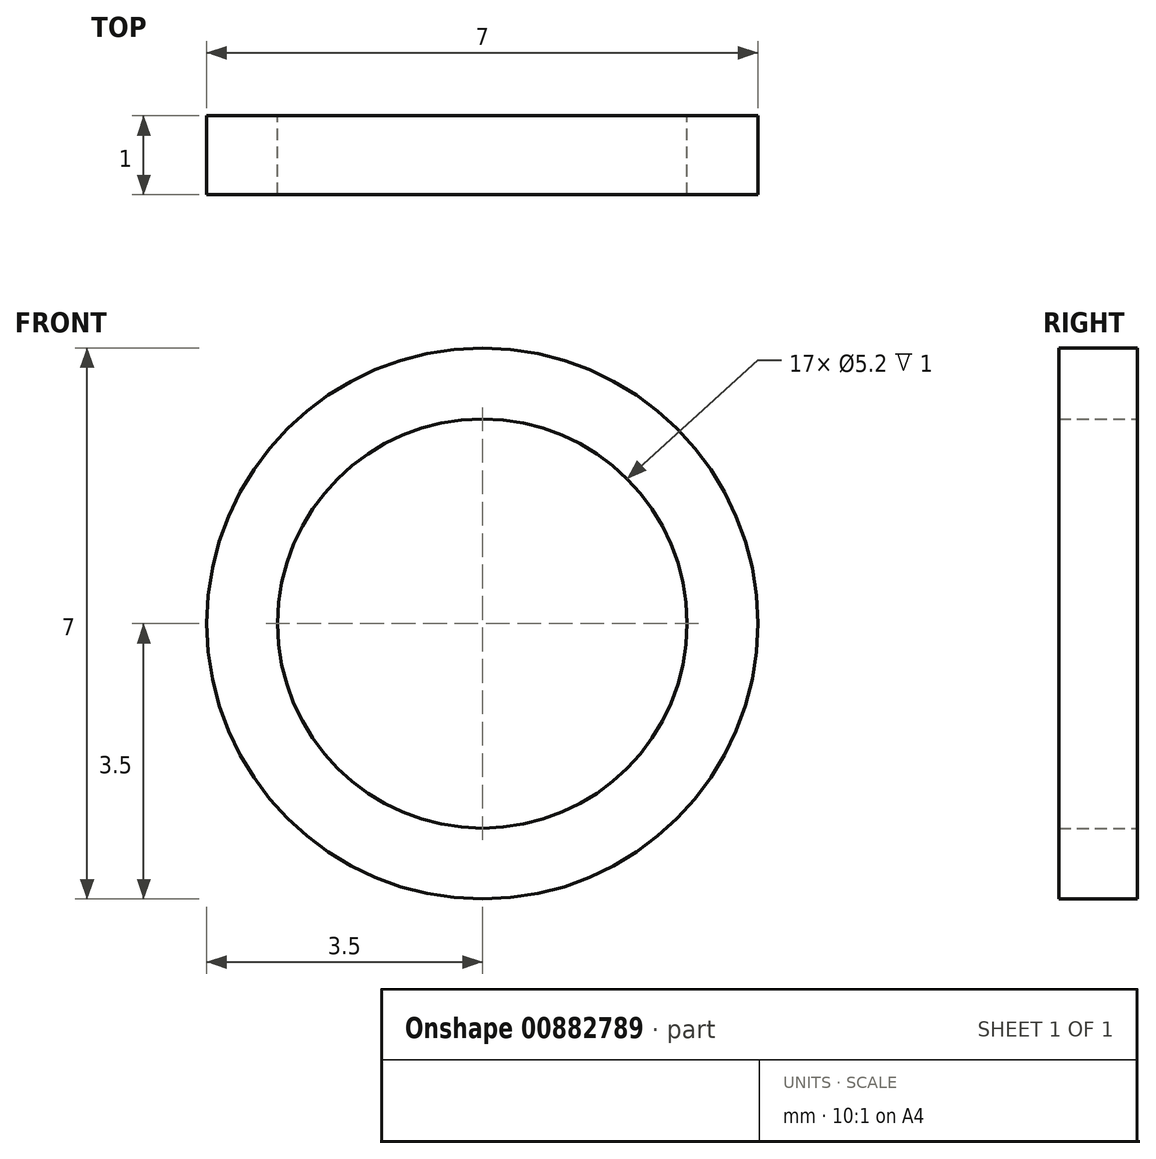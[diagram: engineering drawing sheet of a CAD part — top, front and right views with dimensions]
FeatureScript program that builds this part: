
annotation { "Feature Type Name" : "Feature", "Feature Type Description" : "" }
export const myFeature = defineFeature(function(context is Context, id is Id, definition is map)
    precondition{}
    {
        {
            var Q0;
            Q0=qCreatedBy(makeId("Front.planeOp"),FACE);
            var sketch = newSketch(context, id + "F0", { "sketchPlane" : qUnion([Q0])});
            skCircle(sketch, "E0", {"center": v(0, 0) * mm, "radius": 3.5 * mm});
            skCircle(sketch, "E1", {"center": v(0, 0) * mm, "radius": 2.6 * mm});
            skSolve(sketch);
        }
        {
            var Q0;
            Q0 = qSketchRegion(id + "F0", true);
            extrude(context, id + "F1", {"entities" : qUnion([Q0]), "depth" : 1 * mm, "offsetDistance" : 25.4 * mm});
        }
    });
